# Revit family: RS523.x0
name_source: partatom
category: Sanitärinstallationen
units: mm (PartAtom-declared; Revit-internal decimal feet)

## family parameters
Arbeitsebenenbasiert = Nein
Beim Laden mit Abzugskörper schneiden = Nein
Bemaßung runder Anschluss = Durchmesser verwenden
Gemeinsam genutzt = Nein
Immer vertikal = Ja
Raumberechnungspunkt = Nein
Teiletyp = Normal

## types (2) — shared parameters
Baugruppenkennzeichen = D2030300
Hersteller = Resitec
Klebeblech mit Epoxidgrundierung = Ja
RS_AVol-H = 170 mm  [stored 0.557743 ft]
RS_AVol-L = 129 mm  [stored 0.423228 ft]
RS_AVol-T = 129 mm  [stored 0.423228 ft]
RS_DVol-L = 300 mm  [stored 0.984252 ft]
RS_DVol-T = 300 mm  [stored 0.984252 ft]
RS_Manufacture = Resitec
RS_URL = https://resitec.ch
RS_dia001 = 138 mm  [stored 0.452756 ft]
RS_dia002 = 110 mm  [stored 0.360892 ft]
RS_dia10 = 114 mm  [stored 0.374016 ft]
RS_diaRH1 = 150 mm  [stored 0.492126 ft]
RS_dim001 = 75 mm
RS_dim002 = 125 mm  [stored 0.410105 ft]
RS_dim003 = 80 mm  [stored 0.262467 ft]
RS_dim10 = 250 mm  [stored 0.82021 ft]
RS_s001 = 3 mm  [stored 0.00984252 ft]
RS_s002 = 2 mm  [stored 0.00656168 ft]
URL = https://www.resitec.ch
zero-valued in all types: Anschlusswert DU L/s, RS_DN2, Vorgabe-Ansicht

## per-type parameters (varying)
| type | RS_DN1 | RS_DN1d |
| DN60 | 60 mm  [stored 0.19685 ft] | 64 mm |
| DN70 | 70 mm  [stored 0.229659 ft] | 76 mm  [stored 0.249344 ft] |

note: [stored X ft] marks values corroborated as IEEE doubles in the binary element streams (Revit-internal decimal feet)

## geometry (parser evidence)
native form markers: Blend x4
no freeform markers — native parametric forms only
